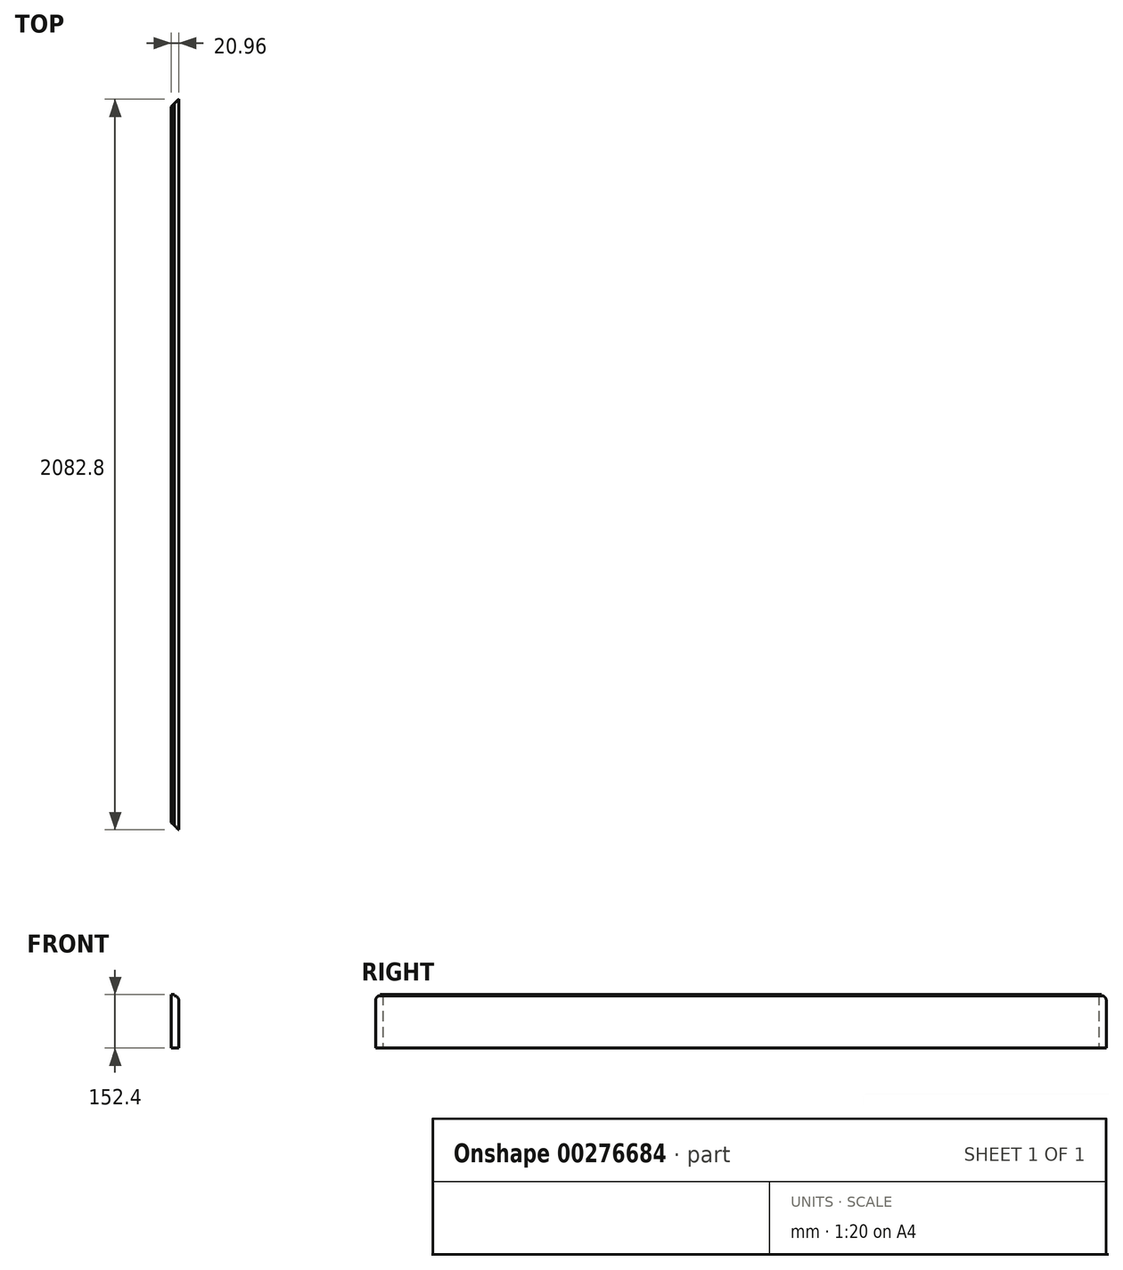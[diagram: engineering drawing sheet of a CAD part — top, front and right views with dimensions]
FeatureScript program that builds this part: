
annotation { "Feature Type Name" : "Feature", "Feature Type Description" : "" }
export const myFeature = defineFeature(function(context is Context, id is Id, definition is map)
    precondition{}
    {
        {
            var Q0;
            Q0=qCreatedBy(makeId("Front.planeOp"),FACE);
            var sketch = newSketch(context, id + "F0", { "sketchPlane" : qUnion([Q0])});
            skLineSegment(sketch, "E0.bottom", {"start": v(0, 0) * mm, "end": v(20.95, 0) * mm});
            skLineSegment(sketch, "E0.top", {"start": v(0, 152.4) * mm, "end": v(8, 152.4) * mm});
            skLineSegment(sketch, "E0.left", {"start": v(0, 0) * mm, "end": v(0, 152.4) * mm});
            skLineSegment(sketch, "E1", {"start": v(8, 152.4) * mm, "end": v(8, 149.22) * mm});
            skLineSegment(sketch, "E2", {"start": v(20.95, 136.53) * mm, "end": v(20.95, 0) * mm});
            skArc(sketch, "E3", {"start": v(20.95, 136.53) * mm, "mid": v(17.15, 145.6) * mm, "end": v(8, 149.22) * mm});
            skSolve(sketch);
        }
        {
            var Q0;
            Q0=makeQuery(id+"F0.imprint","IMPRINT",FACE,{"disambiguationData":[TD([[makeQuery(id+"F0.imprint","IMPRINT",EDGE,{"derivedFrom":sQuery(id+"F0.wireOp",EDGE,"E0.bottom")}),1.0]])]});
            extrude(context, id + "F1", {"entities" : qUnion([Q0]), "oppositeDirection" : true, "depth" : 2082.8 * mm});
        }
        {
            var Q0;
            Q0=makeQuery(id+"F1.opExtrude","SWEPT_FACE",FACE,{"disambiguationData":[OSD([sQuery(id+"F0.wireOp",EDGE,"E0.bottom")])]});
            var sketch = newSketch(context, id + "F2", { "sketchPlane" : qUnion([Q0])});
            skLineSegment(sketch, "E4", {"start": v(20.95, 0) * mm, "end": v(0, -20.95) * mm});
            skSolve(sketch);
        }
        {
            var Q0;
            {var subQ0=sQuery(id+"F2.wireOp",EDGE,"E4");Q0=makeQuery(id+"F2.imprint","IMPRINT",FACE,{"disambiguationData":[TD([[makeQuery(id+"F2.imprint","IMPRINT",EDGE,{"derivedFrom":subQ0}),-1.0]])]});}
            extrude(context, id + "F3", {"entities" : qUnion([Q0]), "operationType" : NewBodyOperationType.REMOVE, "oppositeDirection" : true, "depth" : 152.4 * mm});
        }
        {
            var Q0;
            Q0=makeQuery(id+"F1.opExtrude","SWEPT_FACE",FACE,{"disambiguationData":[OSD([sQuery(id+"F0.wireOp",EDGE,"E0.bottom")])]});
            var sketch = newSketch(context, id + "F4", { "sketchPlane" : qUnion([Q0])});
            skLineSegment(sketch, "E5", {"start": v(20.96, -2082.8) * mm, "end": v(0, -2061.85) * mm});
            skSolve(sketch);
        }
        {
            var Q0;
            {var subQ0=sQuery(id+"F4.wireOp",EDGE,"E5");Q0=makeQuery(id+"F4.imprint","IMPRINT",FACE,{"disambiguationData":[TD([[makeQuery(id+"F4.imprint","IMPRINT",EDGE,{"derivedFrom":subQ0}),1.0]])]});}
            extrude(context, id + "F5", {"entities" : qUnion([Q0]), "operationType" : NewBodyOperationType.REMOVE, "oppositeDirection" : true, "depth" : 152.4 * mm});
        }
    });
